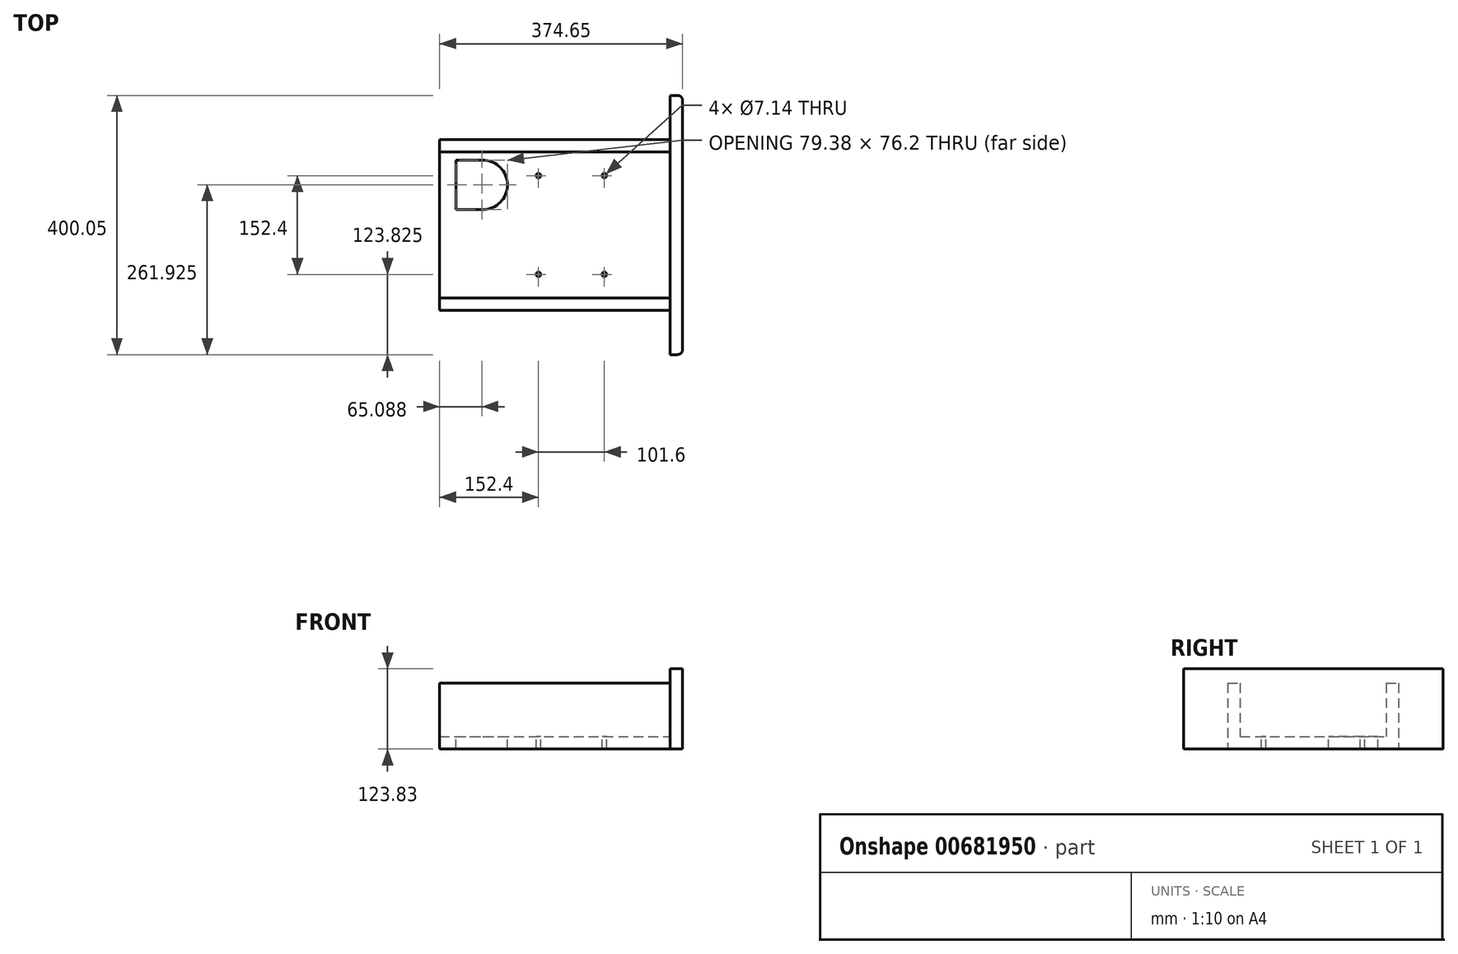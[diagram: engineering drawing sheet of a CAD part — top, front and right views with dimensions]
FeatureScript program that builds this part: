
annotation { "Feature Type Name" : "Feature", "Feature Type Description" : "" }
export const myFeature = defineFeature(function(context is Context, id is Id, definition is map)
    precondition{}
    {
        {
            var Q0;
            Q0=qCreatedBy(makeId("Top.planeOp"),FACE);
            var sketch = newSketch(context, id + "F0", { "sketchPlane" : qUnion([Q0])});
            skLineSegment(sketch, "E0.bottom", {"start": v(0, 0) * mm, "end": v(355.6, 0) * mm});
            skLineSegment(sketch, "E0.top", {"start": v(0, 263.53) * mm, "end": v(355.6, 263.53) * mm});
            skLineSegment(sketch, "E0.left", {"start": v(0, 0) * mm, "end": v(0, 263.53) * mm});
            skLineSegment(sketch, "E0.right", {"start": v(355.6, 0) * mm, "end": v(355.6, 263.53) * mm});
            skLineSegment(sketch, "E1", {"start": v(355.6, 263.53) * mm, "end": v(355.6, 331.8) * mm});
            skLineSegment(sketch, "E2", {"start": v(355.6, 331.8) * mm, "end": v(374.65, 331.8) * mm});
            skLineSegment(sketch, "E3", {"start": v(374.65, 331.8) * mm, "end": v(374.65, -68.25) * mm});
            skLineSegment(sketch, "E4", {"start": v(374.65, -68.25) * mm, "end": v(355.6, -68.25) * mm});
            skLineSegment(sketch, "E5", {"start": v(355.6, -68.25) * mm, "end": v(355.6, 0) * mm});
            skSolve(sketch);
        }
        {
            var Q0;
            Q0=makeQuery(id+"F0.imprint","IMPRINT",FACE,{"disambiguationData":[TD([[makeQuery(id+"F0.imprint","IMPRINT",EDGE,{"derivedFrom":sQuery(id+"F0.wireOp",EDGE,"E0.bottom")}),1.0]])]});
            extrude(context, id + "F1", {"entities" : qUnion([Q0]), "depth" : 19.05 * mm, "offsetDistance" : 25.4 * mm});
        }
        {
            var Q0;
            Q0=makeQuery(id+"F1.opExtrude","CAP_FACE",FACE,{"disambiguationData":[OSD([sQuery(id+"F0.wireOp",EDGE,"E0.bottom"),sQuery(id+"F0.wireOp",EDGE,"E0.top"),sQuery(id+"F0.wireOp",EDGE,"E0.left"),sQuery(id+"F0.wireOp",EDGE,"E0.right")])],"isStart":false});
            var sketch = newSketch(context, id + "F2", { "sketchPlane" : qUnion([Q0])});
            skLineSegment(sketch, "E6.bottom", {"start": v(0, 263.53) * mm, "end": v(355.6, 263.53) * mm});
            skLineSegment(sketch, "E6.top", {"start": v(0, 244.47) * mm, "end": v(355.6, 244.47) * mm});
            skLineSegment(sketch, "E6.left", {"start": v(0, 263.53) * mm, "end": v(0, 244.47) * mm});
            skLineSegment(sketch, "E6.right", {"start": v(355.6, 263.53) * mm, "end": v(355.6, 244.47) * mm});
            skLineSegment(sketch, "E7.bottom", {"start": v(0, 0) * mm, "end": v(355.6, 0) * mm});
            skLineSegment(sketch, "E7.top", {"start": v(0, 19.05) * mm, "end": v(355.6, 19.05) * mm});
            skLineSegment(sketch, "E7.left", {"start": v(0, 0) * mm, "end": v(0, 19.05) * mm});
            skLineSegment(sketch, "E7.right", {"start": v(355.6, 0) * mm, "end": v(355.6, 19.05) * mm});
            skSolve(sketch);
        }
        {
            var Q0;
            {var subQ0=sQuery(id+"F2.wireOp",EDGE,"E6.bottom");Q0=makeQuery(id+"F2.imprint","IMPRINT",FACE,{"disambiguationData":[TD([[makeQuery(id+"F2.imprint","IMPRINT",EDGE,{"derivedFrom":subQ0}),-1.0]])]});}
            var Q1;
            {var subQ0=sQuery(id+"F2.wireOp",EDGE,"E7.bottom");Q1=makeQuery(id+"F2.imprint","IMPRINT",FACE,{"disambiguationData":[TD([[makeQuery(id+"F2.imprint","IMPRINT",EDGE,{"derivedFrom":subQ0}),1.0]])]});}
            extrude(context, id + "F3", {"entities" : qUnion([Q0, Q1]), "operationType" : NewBodyOperationType.ADD, "depth" : 82.55 * mm, "offsetDistance" : 25.4 * mm});
        }
        {
            var Q0;
            Q0=qCreatedBy(makeId("Top.planeOp"),FACE);
            var sketch = newSketch(context, id + "F4", { "sketchPlane" : qUnion([Q0])});
            skLineSegment(sketch, "E8.bottom", {"start": v(355.6, 331.8) * mm, "end": v(374.65, 331.8) * mm});
            skLineSegment(sketch, "E8.top", {"start": v(355.6, -68.25) * mm, "end": v(374.65, -68.25) * mm});
            skLineSegment(sketch, "E8.left", {"start": v(355.6, 331.8) * mm, "end": v(355.6, -68.25) * mm});
            skLineSegment(sketch, "E8.right", {"start": v(374.65, 331.8) * mm, "end": v(374.65, -68.25) * mm});
            skSolve(sketch);
        }
        {
            var Q0;
            Q0=makeQuery(id+"F4.imprint","IMPRINT",FACE,{"disambiguationData":[TD([[makeQuery(id+"F4.imprint","IMPRINT",EDGE,{"derivedFrom":sQuery(id+"F4.wireOp",EDGE,"E8.bottom")}),-1.0]])]});
            extrude(context, id + "F5", {"entities" : qUnion([Q0]), "operationType" : NewBodyOperationType.ADD, "depth" : 123.82 * mm, "offsetDistance" : 25.4 * mm});
        }
        {
            var Q0;
            Q0=makeQuery(id+"F5.opExtrude","SWEPT_EDGE",EDGE,{"disambiguationData":[OSD([sQuery(id+"F4.wireOp",EDGE,"E8.bottom"),sQuery(id+"F4.wireOp",EDGE,"E8.right")])]});
            var Q1;
            Q1=makeQuery(id+"F5.opExtrude","SWEPT_EDGE",EDGE,{"disambiguationData":[OSD([sQuery(id+"F4.wireOp",EDGE,"E8.top"),sQuery(id+"F4.wireOp",EDGE,"E8.right")])]});
            fillet(context, id + "F6", {"entities" : qUnion([Q0, Q1]), "radius" : 7.94 * mm, "tangentPropagation" : true, "allowEdgeOverflow" : false});
        }
        {
            var Q0;
            Q0=makeQuery(id+"F1.opExtrude","CAP_FACE",FACE,{"disambiguationData":[OSD([sQuery(id+"F0.wireOp",EDGE,"E0.bottom"),sQuery(id+"F0.wireOp",EDGE,"E0.top"),sQuery(id+"F0.wireOp",EDGE,"E0.left"),sQuery(id+"F0.wireOp",EDGE,"E0.right")])],"isStart":false});
            var sketch = newSketch(context, id + "F7", { "sketchPlane" : qUnion([Q0])});
            skLineSegment(sketch, "E9", {"start": v(25.4, 231.78) * mm, "end": v(25.4, 155.58) * mm});
            skLineSegment(sketch, "E10", {"start": v(25.4, 155.58) * mm, "end": v(66.68, 155.58) * mm});
            skLineSegment(sketch, "E11", {"start": v(25.4, 231.78) * mm, "end": v(66.68, 231.78) * mm});
            skArc(sketch, "E12", {"start": v(66.68, 155.57) * mm, "mid": v(104.78, 193.67) * mm, "end": v(66.68, 231.77) * mm});
            skSolve(sketch);
        }
        {
            var Q0;
            Q0 = qSketchRegion(id + "F7", true);
            extrude(context, id + "F8", {"entities" : qUnion([Q0]), "operationType" : NewBodyOperationType.REMOVE, "oppositeDirection" : true, "depth" : 25.4 * mm, "offsetDistance" : 25.4 * mm});
        }
        {
            var Q0;
            Q0=makeQuery(id+"F1.opExtrude","CAP_FACE",FACE,{"disambiguationData":[OSD([sQuery(id+"F0.wireOp",EDGE,"E0.bottom"),sQuery(id+"F0.wireOp",EDGE,"E0.top"),sQuery(id+"F0.wireOp",EDGE,"E0.left"),sQuery(id+"F0.wireOp",EDGE,"E0.right")])],"isStart":false});
            var sketch = newSketch(context, id + "F9", { "sketchPlane" : qUnion([Q0])});
            skCircle(sketch, "E13", {"center": v(152.4, 207.98) * mm, "radius": 3.57 * mm});
            skCircle(sketch, "E14", {"center": v(152.4, 55.58) * mm, "radius": 3.57 * mm});
            skCircle(sketch, "E15", {"center": v(254, 207.98) * mm, "radius": 3.57 * mm});
            skCircle(sketch, "E16", {"center": v(254, 55.58) * mm, "radius": 3.57 * mm});
            skLineSegment(sketch, "E17", {"start": v(0, 131.78) * mm, "end": v(398.15, 131.78) * mm});
            skSolve(sketch);
        }
        {
            var Q0;
            Q0 = qSketchRegion(id + "F9", true);
            extrude(context, id + "F10", {"entities" : qUnion([Q0]), "operationType" : NewBodyOperationType.REMOVE, "oppositeDirection" : true, "depth" : 25.4 * mm, "offsetDistance" : 25.4 * mm});
        }
    });
